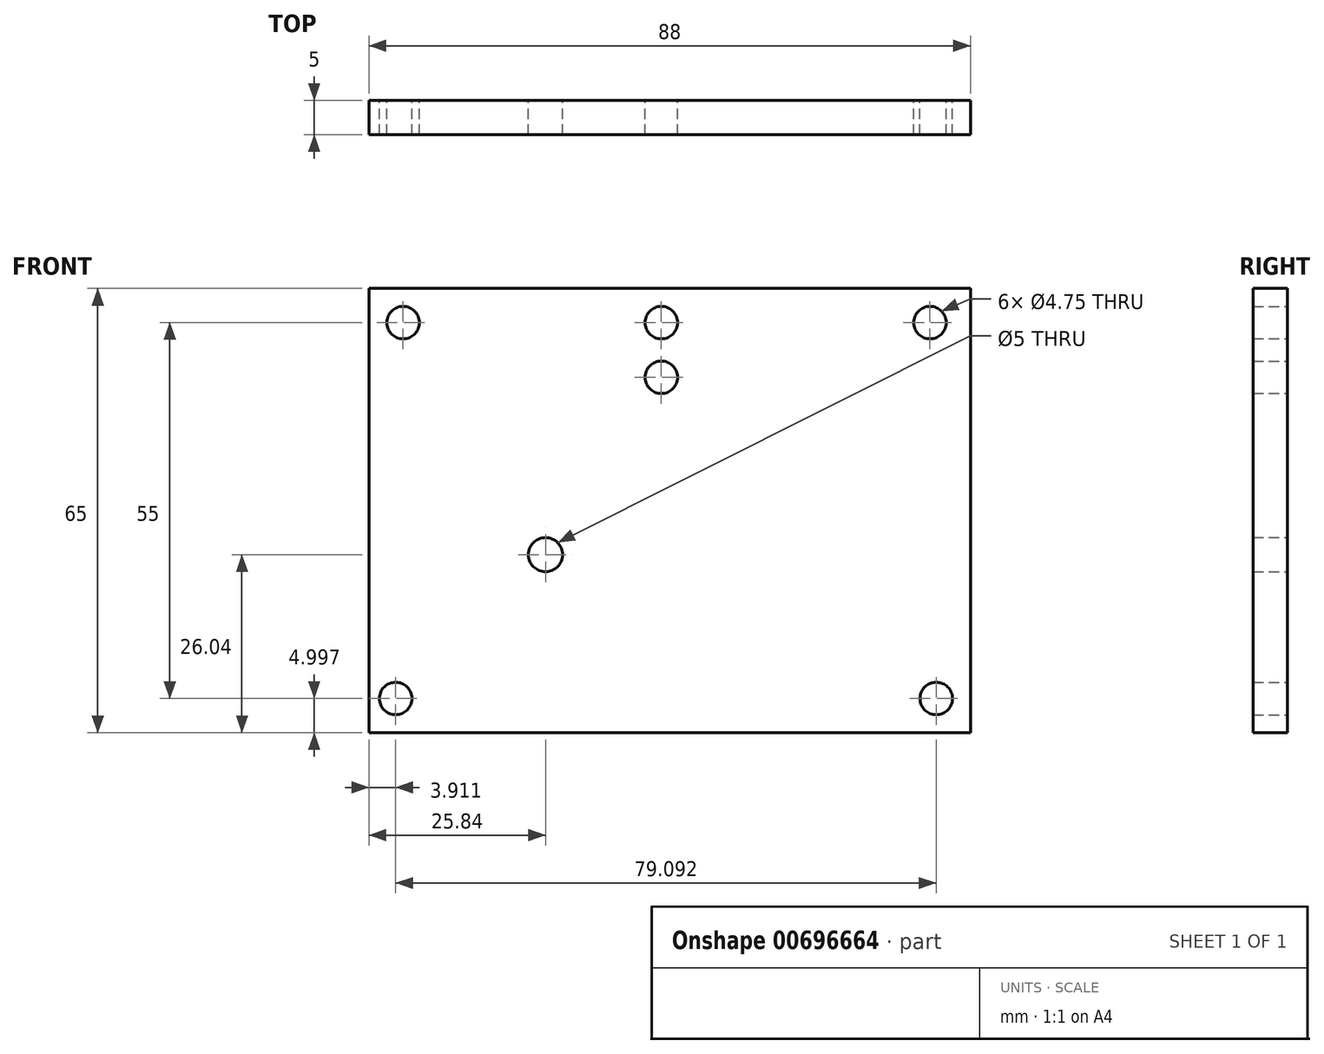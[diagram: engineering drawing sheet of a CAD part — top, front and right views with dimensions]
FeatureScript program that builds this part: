
annotation { "Feature Type Name" : "Feature", "Feature Type Description" : "" }
export const myFeature = defineFeature(function(context is Context, id is Id, definition is map)
    precondition{}
    {
        {
            var Q0;
            Q0=qCreatedBy(makeId("Front.planeOp"),FACE);
            var sketch = newSketch(context, id + "F0", { "sketchPlane" : qUnion([Q0])});
            skCircle(sketch, "E0", {"center": v(0, 0) * mm, "radius": 5 * mm});
            skLineSegment(sketch, "E1.bottom", {"start": v(-27.87, 43.11) * mm, "end": v(33.76, 43.11) * mm});
            skLineSegment(sketch, "E1.top", {"start": v(-32.87, -51.5) * mm, "end": v(38.76, -51.5) * mm});
            skLineSegment(sketch, "E1.left", {"start": v(-32.87, 38.11) * mm, "end": v(-32.87, -51.5) * mm});
            skLineSegment(sketch, "E1.right", {"start": v(38.76, 38.11) * mm, "end": v(38.76, -51.5) * mm});
            skLineSegment(sketch, "E2.bottom", {"start": v(-1.35, 43.11) * mm, "end": v(2.24, 43.11) * mm});
            skLineSegment(sketch, "E2.top", {"start": v(-1.35, -51.5) * mm, "end": v(2.24, -51.5) * mm});
            skLineSegment(sketch, "E2.left", {"start": v(-6.35, 38.11) * mm, "end": v(-6.35, -46.5) * mm});
            skLineSegment(sketch, "E2.right", {"start": v(7.24, 38.11) * mm, "end": v(7.24, -46.5) * mm});
            skLineSegment(sketch, "E3.bottom", {"start": v(-32.87, 38.4) * mm, "end": v(22.96, 38.4) * mm});
            skLineSegment(sketch, "E3.top", {"start": v(-32.87, -51.5) * mm, "end": v(22.96, -51.5) * mm});
            skLineSegment(sketch, "E3.left", {"start": v(-32.87, 38.4) * mm, "end": v(-32.87, -51.5) * mm});
            skLineSegment(sketch, "E3.right", {"start": v(27.96, 33.4) * mm, "end": v(27.96, -46.5) * mm});
            skLineSegment(sketch, "E4.bottom", {"start": v(-16.2, 38.4) * mm, "end": v(38.76, 38.4) * mm});
            skLineSegment(sketch, "E4.top", {"start": v(-16.2, -51.5) * mm, "end": v(38.76, -51.5) * mm});
            skLineSegment(sketch, "E4.left", {"start": v(-21.2, 33.4) * mm, "end": v(-21.2, -46.5) * mm});
            skLineSegment(sketch, "E4.right", {"start": v(38.76, 38.4) * mm, "end": v(38.76, -51.5) * mm});
            skLineSegment(sketch, "E5.bottom", {"start": v(-32.87, -34.37) * mm, "end": v(33.76, -34.37) * mm});
            skLineSegment(sketch, "E5.left", {"start": v(-32.87, -34.37) * mm, "end": v(-32.87, -51.5) * mm});
            skLineSegment(sketch, "E5.right", {"start": v(38.76, -39.37) * mm, "end": v(38.76, -51.5) * mm});
            skLineSegment(sketch, "E6.bottom", {"start": v(-27.87, 15.98) * mm, "end": v(33.76, 15.98) * mm});
            skLineSegment(sketch, "E6.top", {"start": v(-27.87, -15.04) * mm, "end": v(33.76, -15.04) * mm});
            skLineSegment(sketch, "E6.left", {"start": v(-32.87, 10.98) * mm, "end": v(-32.87, -10.04) * mm});
            skLineSegment(sketch, "E6.right", {"start": v(38.76, 10.98) * mm, "end": v(38.76, -10.04) * mm});
            skPoint(sketch, "E7.visualSharp", {"position": v(-21.2, 38.4) * mm});
            skArc(sketch, "E7.filletArc", {"start": v(-16.2, 38.4) * mm, "mid": v(-19.73, 36.93) * mm, "end": v(-21.2, 33.4) * mm});
            skPoint(sketch, "E8.visualSharp", {"position": v(27.96, 38.4) * mm});
            skArc(sketch, "E8.filletArc", {"start": v(27.96, 33.4) * mm, "mid": v(26.5, 36.93) * mm, "end": v(22.96, 38.4) * mm});
            skPoint(sketch, "E9.visualSharp", {"position": v(38.76, -34.37) * mm});
            skArc(sketch, "E9.filletArc", {"start": v(38.76, -39.37) * mm, "mid": v(37.3, -35.84) * mm, "end": v(33.76, -34.37) * mm});
            skPoint(sketch, "E10.visualSharp", {"position": v(38.76, -15.04) * mm});
            skArc(sketch, "E10.filletArc", {"start": v(33.76, -15.04) * mm, "mid": v(37.3, -13.58) * mm, "end": v(38.76, -10.04) * mm});
            skPoint(sketch, "E11.visualSharp", {"position": v(38.76, 15.98) * mm});
            skArc(sketch, "E11.filletArc", {"start": v(38.76, 10.98) * mm, "mid": v(37.3, 14.51) * mm, "end": v(33.76, 15.98) * mm});
            skPoint(sketch, "E12.visualSharp", {"position": v(-32.87, 15.98) * mm});
            skArc(sketch, "E12.filletArc", {"start": v(-27.87, 15.98) * mm, "mid": v(-31.4, 14.51) * mm, "end": v(-32.87, 10.98) * mm});
            skPoint(sketch, "E13.visualSharp", {"position": v(-32.87, -15.04) * mm});
            skArc(sketch, "E13.filletArc", {"start": v(-32.87, -10.04) * mm, "mid": v(-31.4, -13.58) * mm, "end": v(-27.87, -15.04) * mm});
            skPoint(sketch, "E14.visualSharp", {"position": v(-32.87, 43.11) * mm});
            skArc(sketch, "E14.filletArc", {"start": v(-27.87, 43.11) * mm, "mid": v(-31.4, 41.65) * mm, "end": v(-32.87, 38.11) * mm});
            skPoint(sketch, "E15.visualSharp", {"position": v(38.76, 43.11) * mm});
            skArc(sketch, "E15.filletArc", {"start": v(38.76, 38.11) * mm, "mid": v(37.3, 41.65) * mm, "end": v(33.76, 43.11) * mm});
            skPoint(sketch, "E16.visualSharp", {"position": v(-21.2, -51.5) * mm});
            skArc(sketch, "E16.filletArc", {"start": v(-21.2, -46.5) * mm, "mid": v(-19.73, -50.04) * mm, "end": v(-16.2, -51.5) * mm});
            skPoint(sketch, "E17.visualSharp", {"position": v(-6.35, -51.5) * mm});
            skArc(sketch, "E17.filletArc", {"start": v(-6.35, -46.5) * mm, "mid": v(-4.89, -50.04) * mm, "end": v(-1.35, -51.5) * mm});
            skPoint(sketch, "E18.visualSharp", {"position": v(7.24, -51.5) * mm});
            skArc(sketch, "E18.filletArc", {"start": v(2.24, -51.5) * mm, "mid": v(5.78, -50.04) * mm, "end": v(7.24, -46.5) * mm});
            skPoint(sketch, "E19.visualSharp", {"position": v(27.96, -51.5) * mm});
            skArc(sketch, "E19.filletArc", {"start": v(22.96, -51.5) * mm, "mid": v(26.5, -50.04) * mm, "end": v(27.96, -46.5) * mm});
            skPoint(sketch, "E20.visualSharp", {"position": v(-6.35, 43.11) * mm});
            skArc(sketch, "E20.filletArc", {"start": v(-1.35, 43.11) * mm, "mid": v(-4.89, 41.65) * mm, "end": v(-6.35, 38.11) * mm});
            skPoint(sketch, "E21.visualSharp", {"position": v(7.24, 43.11) * mm});
            skArc(sketch, "E21.filletArc", {"start": v(7.24, 38.11) * mm, "mid": v(5.78, 41.65) * mm, "end": v(2.24, 43.11) * mm});
            skLineSegment(sketch, "E22.bottom", {"start": v(-33.04, 6.73) * mm, "end": v(38.76, 6.73) * mm});
            skLineSegment(sketch, "E22.top", {"start": v(-33.04, -6.7) * mm, "end": v(38.76, -6.7) * mm});
            skLineSegment(sketch, "E22.left", {"start": v(-33.04, 6.73) * mm, "end": v(-33.04, -6.7) * mm});
            skLineSegment(sketch, "E22.right", {"start": v(38.76, 6.73) * mm, "end": v(38.76, -6.7) * mm});
            skLineSegment(sketch, "E23.bottom", {"start": v(20.68, -6.7) * mm, "end": v(20.9, -6.7) * mm});
            skLineSegment(sketch, "E23.top", {"start": v(20.68, -6.7) * mm, "end": v(20.9, -6.7) * mm});
            skLineSegment(sketch, "E23.left", {"start": v(20.68, -6.7) * mm, "end": v(20.68, -6.7) * mm});
            skLineSegment(sketch, "E23.right", {"start": v(20.9, -6.7) * mm, "end": v(20.9, -6.7) * mm});
            skSolve(sketch);
        }
        {
            var Q0;
            Q0=qCreatedBy(makeId("Front.planeOp"),FACE);
            var sketch = newSketch(context, id + "F1", { "sketchPlane" : qUnion([Q0])});
            skFitSpline(sketch, "E24", {"points": [v(0, 44.82) * mm, v(-14.33, 46.48) * mm, v(-14.7, 61.1) * mm, v(-28.2, 69.63) * mm, v(-36.15, 65.99) * mm, v(-26.08, 56.96) * mm, v(-33.77, 36.88) * mm, v(-31.1, 33.45) * mm, v(-15.43, 23.2) * mm, v(-14.37, 9.46) * mm, v(-15.11, -2.39) * mm, v(-15.55, -9.56) * mm, v(-30.41, -28.54) * mm, v(-37.48, -43.44) * mm, v(-38.64, -53.89) * mm, v(0, -46.8) * mm, v(16.62, -45.09) * mm, v(31.79, -46.15) * mm, v(50.3, -47.94) * mm, v(47.65, -24.25) * mm, v(36.43, -22.22) * mm, v(31.76, 0) * mm, v(36.47, 11.05) * mm, v(47.5, 23.74) * mm, v(53.4, 25.12) * mm, v(61.1, 33.99) * mm, v(51.66, 48.28) * mm, v(20.89, 42.3) * mm, v(5.74, 38.06) * mm, v(0, 44.82) * mm]});
            skLineSegment(sketch, "E25.bottom", {"start": v(47.1, -49.6) * mm, "end": v(62.78, -49.6) * mm});
            skLineSegment(sketch, "E25.top", {"start": v(47.1, -23.86) * mm, "end": v(62.78, -23.86) * mm});
            skLineSegment(sketch, "E25.left", {"start": v(47.1, -49.6) * mm, "end": v(47.1, -23.86) * mm});
            skLineSegment(sketch, "E25.right", {"start": v(65.78, -46.6) * mm, "end": v(65.78, -26.86) * mm});
            skLineSegment(sketch, "E26.bottom", {"start": v(47.1, 23.5) * mm, "end": v(62.78, 23.5) * mm});
            skLineSegment(sketch, "E26.top", {"start": v(47.1, 49.24) * mm, "end": v(62.78, 49.24) * mm});
            skLineSegment(sketch, "E26.left", {"start": v(47.1, 23.5) * mm, "end": v(47.1, 49.24) * mm});
            skLineSegment(sketch, "E26.right", {"start": v(65.78, 26.5) * mm, "end": v(65.78, 46.24) * mm});
            skLineSegment(sketch, "E27", {"start": v(47.1, -23.86) * mm, "end": v(47.1, 23.5) * mm, "construction": true});
            skFitSpline(sketch, "E28", {"points": [v(-18.56, 41.06) * mm, v(0, 38.9) * mm, v(0, 22.4) * mm, v(-5.06, 14.44) * mm, v(-11.21, 28.47) * mm, v(-21.4, 35.51) * mm, v(-28.94, 42.11) * mm, v(-18.56, 41.06) * mm]});
            skFitSpline(sketch, "E29", {"points": [v(14.4, 30) * mm, v(39.64, 39.9) * mm, v(47.1, 36.38) * mm, v(36.13, 27.42) * mm, v(21.1, 9.74) * mm, v(10.06, 4.32) * mm, v(14.4, 30) * mm]});
            skFitSpline(sketch, "E30", {"points": [v(11.6, -5.4) * mm, v(22.92, 0) * mm, v(30.81, -22.85) * mm, v(39.8, -31.1) * mm, v(38.94, -41.17) * mm, v(10.95, -35.8) * mm, v(11.6, -5.4) * mm]});
            skFitSpline(sketch, "E31", {"points": [v(-22.27, -45.97) * mm, v(-32.01, -43.44) * mm, v(-8.2, -10.57) * mm, v(0, -10.68) * mm, v(0, -39.48) * mm, v(-22.27, -45.97) * mm]});
            skCircle(sketch, "E32", {"center": v(-28.14, 65.1) * mm, "radius": 2.5 * mm});
            skCircle(sketch, "E33", {"center": v(-35.27, -48.88) * mm, "radius": 2.5 * mm});
            skPoint(sketch, "E34.visualSharp", {"position": v(65.78, -23.86) * mm});
            skArc(sketch, "E34.filletArc", {"start": v(65.78, -26.86) * mm, "mid": v(64.9, -24.74) * mm, "end": v(62.78, -23.86) * mm});
            skPoint(sketch, "E35.visualSharp", {"position": v(65.78, -49.6) * mm});
            skArc(sketch, "E35.filletArc", {"start": v(62.78, -49.6) * mm, "mid": v(64.9, -48.72) * mm, "end": v(65.78, -46.6) * mm});
            skPoint(sketch, "E36.visualSharp", {"position": v(65.78, 23.5) * mm});
            skArc(sketch, "E36.filletArc", {"start": v(62.78, 23.5) * mm, "mid": v(64.9, 24.39) * mm, "end": v(65.78, 26.5) * mm});
            skPoint(sketch, "E37.visualSharp", {"position": v(65.78, 49.24) * mm});
            skArc(sketch, "E37.filletArc", {"start": v(65.78, 46.24) * mm, "mid": v(64.9, 48.36) * mm, "end": v(62.78, 49.24) * mm});
            skCircle(sketch, "E38", {"center": v(52.41, -36.73) * mm, "radius": 2.5 * mm});
            skPoint(sketch, "E38.centerSnap0", {"position": v(47.1, -36.73) * mm});
            skCircle(sketch, "E39", {"center": v(53.4, 36.38) * mm, "radius": 2.5 * mm});
            skCircle(sketch, "E40", {"center": v(0, 0) * mm, "radius": 5 * mm});
            skSolve(sketch);
        }
        {
            var Q0;
            Q0=qCreatedBy(makeId("Front.planeOp"),FACE);
            var sketch = newSketch(context, id + "F2", { "sketchPlane" : qUnion([Q0])});
            skLineSegment(sketch, "E41.bottom", {"start": v(-25.84, -26.04) * mm, "end": v(62.16, -26.04) * mm});
            skLineSegment(sketch, "E41.top", {"start": v(-25.84, 38.96) * mm, "end": v(62.16, 38.96) * mm});
            skLineSegment(sketch, "E41.left", {"start": v(-25.84, -26.04) * mm, "end": v(-25.84, 38.96) * mm});
            skLineSegment(sketch, "E41.right", {"start": v(62.16, -26.04) * mm, "end": v(62.16, 38.96) * mm});
            skCircle(sketch, "E42", {"center": v(-21.93, -21.04) * mm, "radius": 2.38 * mm});
            skCircle(sketch, "E43", {"center": v(-20.84, 33.96) * mm, "radius": 2.38 * mm});
            skCircle(sketch, "E44", {"center": v(57.16, -21.04) * mm, "radius": 2.38 * mm});
            skCircle(sketch, "E45", {"center": v(0, 0) * mm, "radius": 2.5 * mm});
            skCircle(sketch, "E46", {"center": v(16.94, 25.96) * mm, "radius": 2.38 * mm});
            skCircle(sketch, "E47", {"center": v(16.94, 33.96) * mm, "radius": 2.38 * mm});
            skCircle(sketch, "E48", {"center": v(56.25, 33.96) * mm, "radius": 2.38 * mm});
            skSolve(sketch);
        }
        {
            var Q0;
            Q0=makeQuery(id+"F2.imprint","IMPRINT",FACE,{"disambiguationData":[TD([[makeQuery(id+"F2.imprint","IMPRINT",EDGE,{"derivedFrom":sQuery(id+"F2.wireOp",EDGE,"E41.bottom")}),1.0]])]});
            extrude(context, id + "F3", {"entities" : qUnion([Q0]), "depth" : 5 * mm, "offsetDistance" : 25 * mm});
        }
    });
